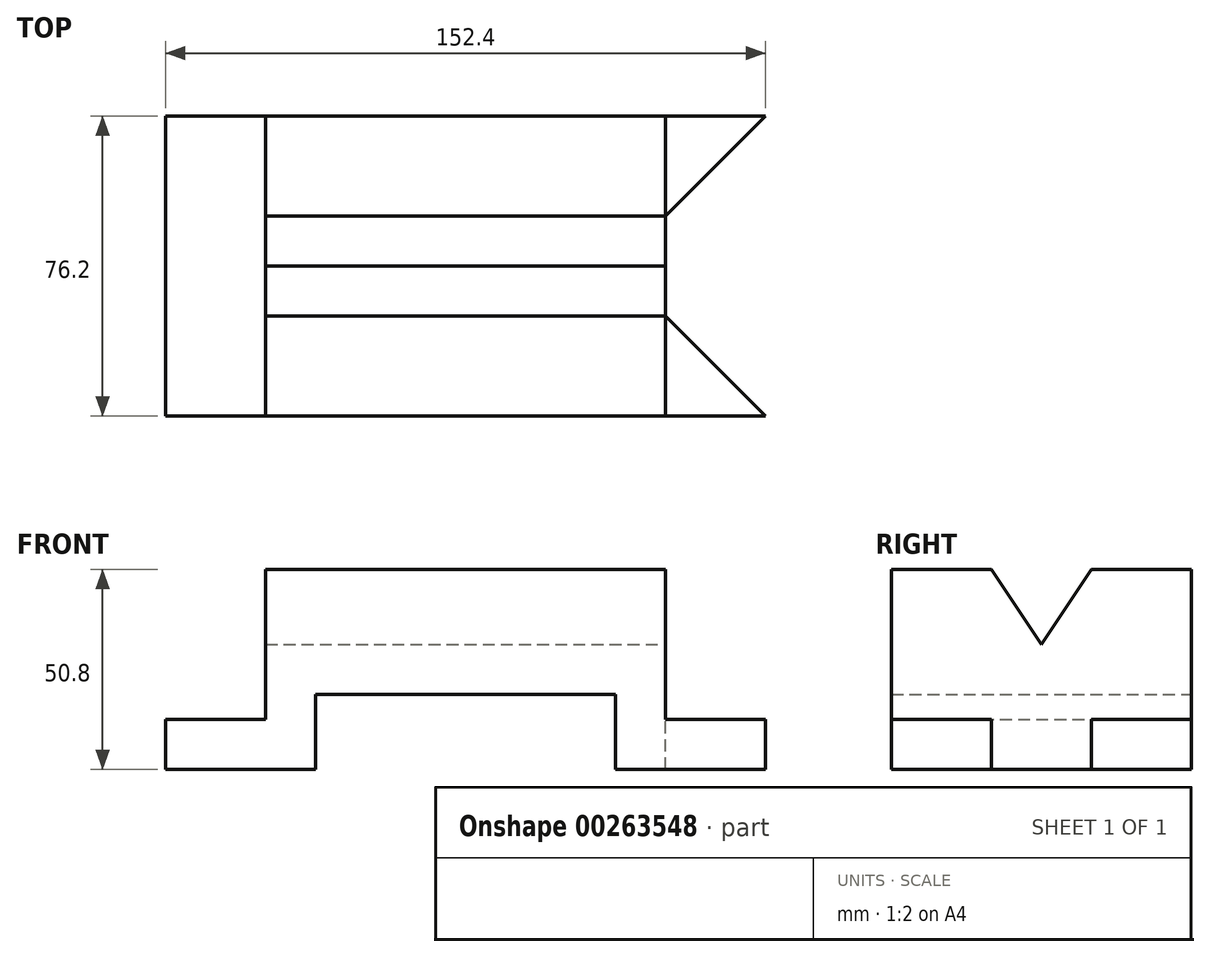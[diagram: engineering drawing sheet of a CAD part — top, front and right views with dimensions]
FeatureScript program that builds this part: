
annotation { "Feature Type Name" : "Feature", "Feature Type Description" : "" }
export const myFeature = defineFeature(function(context is Context, id is Id, definition is map)
    precondition{}
    {
        {
            var Q0;
            Q0=qCreatedBy(makeId("Front.planeOp"),FACE);
            var sketch = newSketch(context, id + "F0", { "sketchPlane" : qUnion([Q0])});
            skLineSegment(sketch, "E0", {"start": v(-64.18, 0) * mm, "end": v(-64.18, -12.7) * mm});
            skLineSegment(sketch, "E1", {"start": v(-64.18, -12.7) * mm, "end": v(-26.08, -12.7) * mm});
            skLineSegment(sketch, "E2", {"start": v(-26.08, -12.7) * mm, "end": v(-26.08, 6.35) * mm});
            skLineSegment(sketch, "E3", {"start": v(-26.08, 6.35) * mm, "end": v(50.12, 6.35) * mm});
            skLineSegment(sketch, "E4", {"start": v(50.12, 6.35) * mm, "end": v(50.12, -12.7) * mm});
            skLineSegment(sketch, "E5", {"start": v(50.12, -12.7) * mm, "end": v(88.22, -12.7) * mm});
            skLineSegment(sketch, "E6", {"start": v(88.22, -12.7) * mm, "end": v(88.22, 0) * mm});
            skLineSegment(sketch, "E7", {"start": v(-64.18, 0) * mm, "end": v(-38.78, 0) * mm});
            skLineSegment(sketch, "E8", {"start": v(-38.78, 0) * mm, "end": v(-38.78, 38.1) * mm});
            skLineSegment(sketch, "E9", {"start": v(-38.78, 38.1) * mm, "end": v(50.12, 38.1) * mm});
            skLineSegment(sketch, "E10", {"start": v(88.22, 0) * mm, "end": v(62.82, 0) * mm});
            skLineSegment(sketch, "E11", {"start": v(62.82, 0) * mm, "end": v(62.82, 38.1) * mm});
            skLineSegment(sketch, "E12", {"start": v(62.82, 38.1) * mm, "end": v(50.12, 38.1) * mm});
            skSolve(sketch);
        }
        {
            var Q0;
            Q0=makeQuery(id+"F0.imprint","IMPRINT",FACE,{"disambiguationData":[TD([[makeQuery(id+"F0.imprint","IMPRINT",EDGE,{"derivedFrom":sQuery(id+"F0.wireOp",EDGE,"E0")}),1.0]])]});
            extrude(context, id + "F1", {"entities" : qUnion([Q0]), "depth" : 76.2 * mm});
        }
        {
            var Q0;
            Q0=makeQuery(id+"F1.opExtrude","SWEPT_FACE",FACE,{"disambiguationData":[OSD([sQuery(id+"F0.wireOp",EDGE,"E10")])]});
            var sketch = newSketch(context, id + "F2", { "sketchPlane" : qUnion([Q0])});
            skLineSegment(sketch, "E13", {"start": v(62.82, -76.2) * mm, "end": v(62.82, -50.8) * mm});
            skLineSegment(sketch, "E14", {"start": v(62.82, -50.8) * mm, "end": v(88.22, -76.2) * mm});
            skLineSegment(sketch, "E15", {"start": v(62.82, 0) * mm, "end": v(62.82, -25.4) * mm});
            skLineSegment(sketch, "E16", {"start": v(62.82, -25.4) * mm, "end": v(88.22, 0) * mm});
            skSolve(sketch);
        }
        {
            var Q0;
            {var subQ0=sQuery(id+"F2.wireOp",EDGE,"E14");Q0=makeQuery(id+"F2.imprint","IMPRINT",FACE,{"disambiguationData":[TD([[makeQuery(id+"F2.imprint","IMPRINT",EDGE,{"derivedFrom":subQ0}),1.0]])]});}
            extrude(context, id + "F3", {"entities" : qUnion([Q0]), "operationType" : NewBodyOperationType.REMOVE, "oppositeDirection" : true, "depth" : 12.7 * mm});
        }
        {
            var Q0;
            {var subQ0=sQuery(id+"F0.wireOp",EDGE,"E11");Q0=makeQuery(id+"F3.boolean.opBoolean","MERGE",FACE,{"derivedFrom":[makeQuery(id+"F1.opExtrude","SWEPT_FACE",FACE,{"disambiguationData":[OSD([subQ0])]}),makeQuery(id+"F3.opExtrude","SWEPT_FACE",FACE,{"disambiguationData":[OSD([sQuery(id+"F0.wireOp",EDGE,"E10"),subQ0])]})]});}
            var sketch = newSketch(context, id + "F4", { "sketchPlane" : qUnion([Q0])});
            skLineSegment(sketch, "E17", {"start": v(-76.2, 38.1) * mm, "end": v(-50.8, 38.1) * mm});
            skLineSegment(sketch, "E18", {"start": v(0, 38.1) * mm, "end": v(-25.4, 38.1) * mm});
            skLineSegment(sketch, "E19", {"start": v(-50.8, 38.1) * mm, "end": v(-38.1, 19.05) * mm});
            skLineSegment(sketch, "E20", {"start": v(-25.4, 38.1) * mm, "end": v(-38.1, 19.05) * mm});
            skPoint(sketch, "E21.start.orphan", {"position": v(0, 19.05) * mm});
            skSolve(sketch);
        }
        {
            var Q0;
            {var subQ0=sQuery(id+"F4.wireOp",EDGE,"E19");Q0=makeQuery(id+"F4.imprint","IMPRINT",FACE,{"disambiguationData":[TD([[makeQuery(id+"F4.imprint","IMPRINT",EDGE,{"derivedFrom":subQ0}),1.0]])]});}
            extrude(context, id + "F5", {"entities" : qUnion([Q0]), "operationType" : NewBodyOperationType.REMOVE, "oppositeDirection" : true, "depth" : 152.4 * mm});
        }
    });
